# Revit family: Valve_Diverter_Trim-DXV-Modulus-D35120600_Series
name_source: partatom
category: Plumbing Fixtures
revit_build: Autodesk Revit 2014 (Build: 20130308_1515(x64)
units: mm (PartAtom-declared; Revit-internal decimal feet)

## types (4) — shared parameters
ADA Compliant = Yes
Assembly Code = D2010710
CW Connection = Yes
CWFU = 3
Cold Water Connection Diameter = 1/2"
Default Elevation = 44"
Description = DXV Modulus Pressure Balance Tub/Shower Valve Trim With Diverter
HW Connection = Yes
HWFU = 3
Height = 7 7/16"
Hot Water Connection Diameter = 1/2"
Installation Type = Wall Mounted
Length = 3 11/16"
Manufacturer = DXV
Price = Prices may vary. Please consult Manufacturer Representative for most up-to-date price list.
Product Page URL = https://www.dxv.com
Tun/Shower Rough Valve D35000600.191 = Yes
URL = https://www.dxv.com
Vent Connection = No
WFU = 4
Waste Connection = No
Water Connection Diameter = 1/2"
Width = 7 7/16"

## per-type parameters (varying)
| type | Finish | Material |
| D35120600.100 | Metal-DXV-100-Polished Chrome | Metal-DXV-100-Polished Chrome |
| D35120600.144 | Metal-DXV-144-Brushed Nickel | Metal-DXV-144-Brushed Nickel |
| D35120600.150 | Metal-DXV-150-Platinum Nickel | Metal-DXV-150-Platinum Nickel |
| D35120600.243 | Metal-DXV-243-Matte Black | Metal-DXV-243-Matte Black |

note: column(s) folded — value = type name in every type: Model

## geometry (parser evidence)
native form markers: Sweep x3
no freeform markers — native parametric forms only
